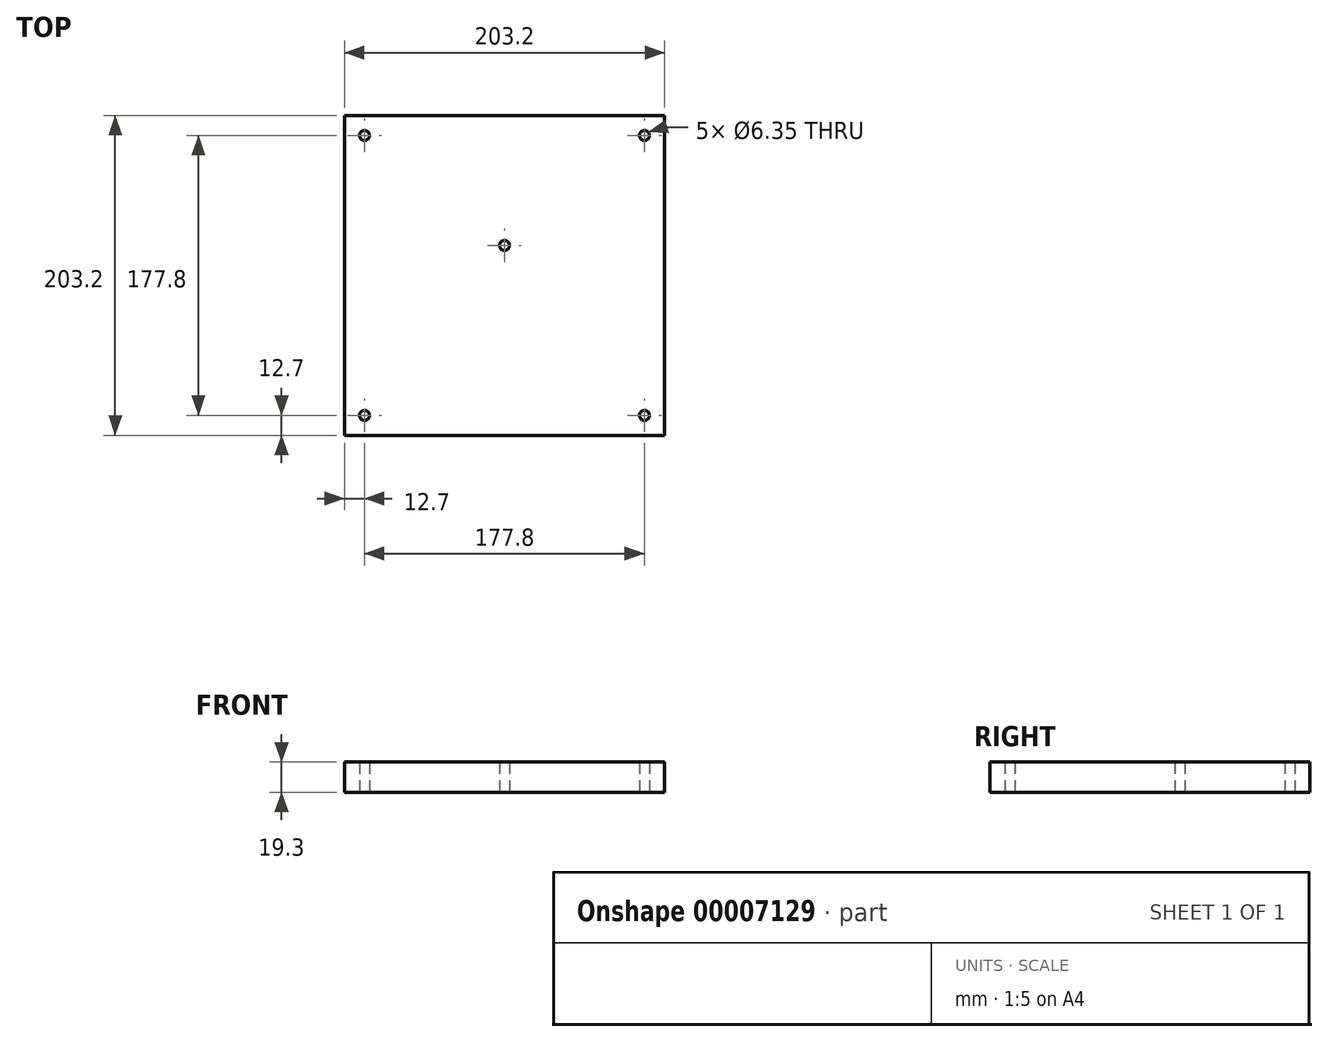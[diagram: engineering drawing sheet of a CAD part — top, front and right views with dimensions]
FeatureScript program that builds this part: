
annotation { "Feature Type Name" : "Feature", "Feature Type Description" : "" }
export const myFeature = defineFeature(function(context is Context, id is Id, definition is map)
    precondition{}
    {
        {
            var Q0;
            Q0=qCreatedBy(makeId("Top.planeOp"),FACE);
            var sketch = newSketch(context, id + "F0", { "sketchPlane" : qUnion([Q0])});
            skLineSegment(sketch, "E0.rect.bottom", {"start": v(101.6, -101.6) * mm, "end": v(-101.6, -101.6) * mm});
            skLineSegment(sketch, "E0.rect.top", {"start": v(101.6, 101.6) * mm, "end": v(-101.6, 101.6) * mm});
            skLineSegment(sketch, "E0.rect.left", {"start": v(101.6, -101.6) * mm, "end": v(101.6, 101.6) * mm});
            skLineSegment(sketch, "E0.rect.right", {"start": v(-101.6, -101.6) * mm, "end": v(-101.6, 101.6) * mm});
            skPoint(sketch, "E0.rect.middle", {"position": v(0, 0) * mm});
            skCircle(sketch, "E1", {"center": v(88.9, 88.9) * mm, "radius": 3.18 * mm});
            skCircle(sketch, "E2", {"center": v(-88.9, 88.9) * mm, "radius": 3.18 * mm});
            skCircle(sketch, "E3", {"center": v(-88.9, -88.9) * mm, "radius": 3.18 * mm});
            skCircle(sketch, "E4", {"center": v(88.9, -88.9) * mm, "radius": 3.18 * mm});
            skLineSegment(sketch, "E5.rect.bottom", {"start": v(88.9, 88.9) * mm, "end": v(-88.9, 88.9) * mm, "construction": true});
            skLineSegment(sketch, "E5.rect.top", {"start": v(88.9, -88.9) * mm, "end": v(-88.9, -88.9) * mm, "construction": true});
            skLineSegment(sketch, "E5.rect.left", {"start": v(88.9, 88.9) * mm, "end": v(88.9, -88.9) * mm, "construction": true});
            skLineSegment(sketch, "E5.rect.right", {"start": v(-88.9, 88.9) * mm, "end": v(-88.9, -88.9) * mm, "construction": true});
            skCircle(sketch, "E6", {"center": v(0, 19.05) * mm, "radius": 3.18 * mm});
            skSolve(sketch);
        }
        {
            var Q0;
            Q0=qSketchRegion(id+"F0",true);
            extrude(context, id + "F1", {"entities" : qUnion([Q0]), "depth" : 19.3 * mm});
        }
        {
            var Q0;
            Q0=makeQuery(id+"F1.opExtrude","CAP_FACE",FACE,{"disambiguationData":[OSD([sQuery(id+"F0.wireOp",EDGE,"E0.rect.bottom"),sQuery(id+"F0.wireOp",EDGE,"E0.rect.top"),sQuery(id+"F0.wireOp",EDGE,"E0.rect.left"),sQuery(id+"F0.wireOp",EDGE,"E0.rect.right"),sQuery(id+"F0.wireOp",EDGE,"E1"),sQuery(id+"F0.wireOp",EDGE,"E2"),sQuery(id+"F0.wireOp",EDGE,"E3"),sQuery(id+"F0.wireOp",EDGE,"E4"),sQuery(id+"F0.wireOp",EDGE,"E6")])],"isStart":true});
            cPlane(context, id + "F2", {"entities" : qUnion([Q0]), "cplaneType" : CPlaneType.OFFSET, "offset" : 5.08 * mm, "oppositeDirection" : true, "width" : 152.4 * mm, "height" : 152.4 * mm});
        }
    });
